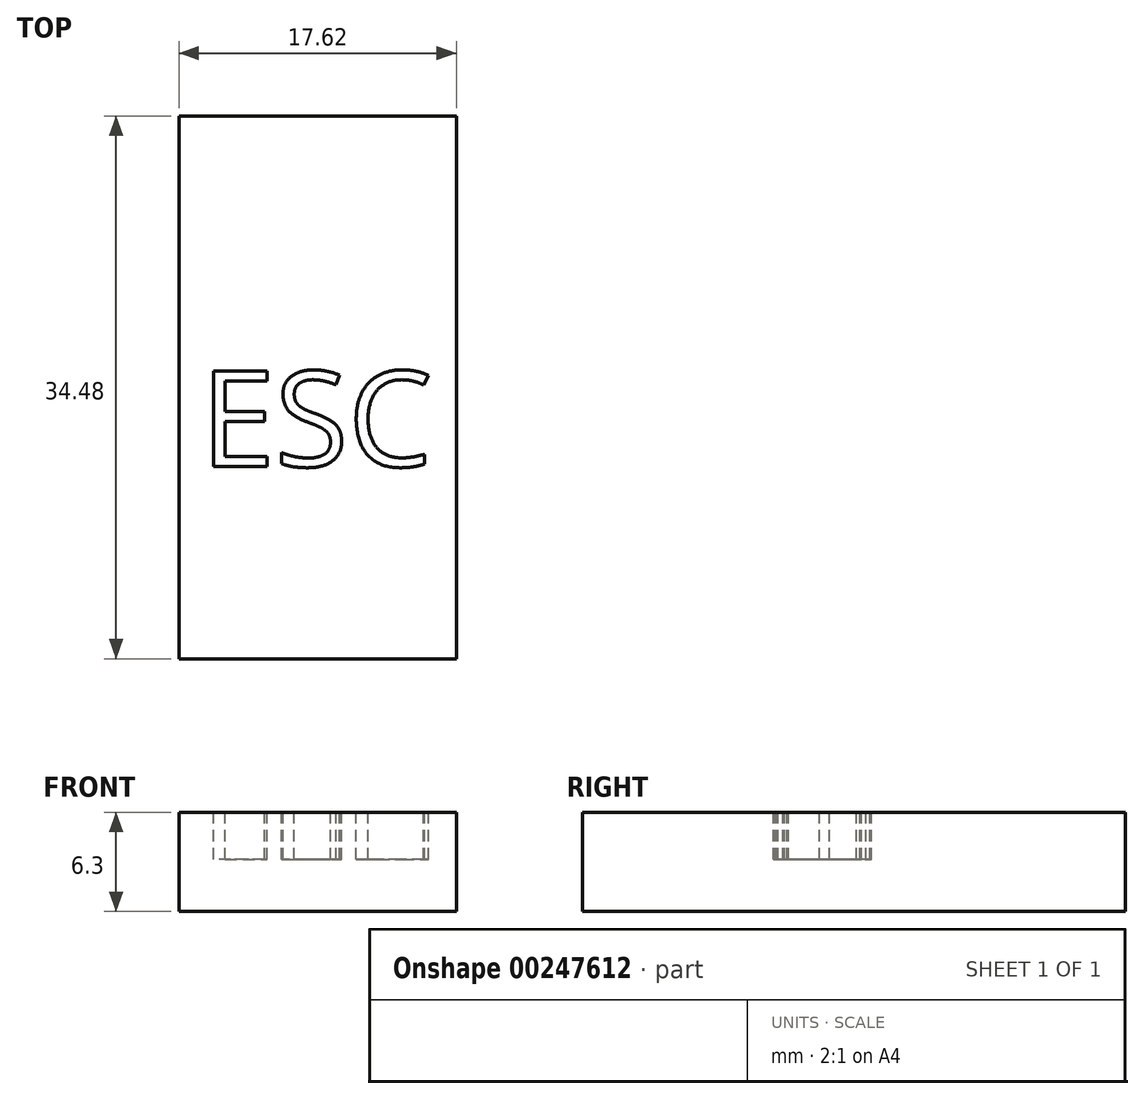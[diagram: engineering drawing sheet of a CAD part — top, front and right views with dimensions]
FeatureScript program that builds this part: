
annotation { "Feature Type Name" : "Feature", "Feature Type Description" : "" }
export const myFeature = defineFeature(function(context is Context, id is Id, definition is map)
    precondition{}
    {
        {
            var Q0;
            Q0=qCreatedBy(makeId("Top.planeOp"),FACE);
            var sketch = newSketch(context, id + "F0", { "sketchPlane" : qUnion([Q0])});
            skLineSegment(sketch, "E0.bottom", {"start": v(-8.8, 17.23) * mm, "end": v(8.81, 17.23) * mm});
            skLineSegment(sketch, "E0.top", {"start": v(-8.81, -17.23) * mm, "end": v(8.8, -17.23) * mm});
            skLineSegment(sketch, "E0.left", {"start": v(-8.8, 17.23) * mm, "end": v(-8.81, -17.23) * mm});
            skLineSegment(sketch, "E0.right", {"start": v(8.81, 17.23) * mm, "end": v(8.8, -17.23) * mm});
            skPoint(sketch, "E0.middle", {"position": v(0, 0) * mm});
            skSolve(sketch);
        }
        {
            var Q0;
            Q0 = qSketchRegion(id + "F0", true);
            extrude(context, id + "F1", {"entities" : qUnion([Q0]), "depth" : 6.3 * mm});
        }
        {
            var Q0;
            Q0=makeQuery(id+"F1.opExtrude","CAP_FACE",FACE,{"disambiguationData":[OSD([sQuery(id+"F0.wireOp",EDGE,"E0.bottom"),sQuery(id+"F0.wireOp",EDGE,"E0.top"),sQuery(id+"F0.wireOp",EDGE,"E0.left"),sQuery(id+"F0.wireOp",EDGE,"E0.right")])],"isStart":false});
            var sketch = newSketch(context, id + "F2", { "sketchPlane" : qUnion([Q0])});
            skText(sketch, "E1", { "text": "ESC", "fontName": "OpenSans-Regular.ttf"});
            const initialGuessF2  = {"E1": [-0.00743, -0.00502, 1, 0, 0.0061]};
            skSetInitialGuess(sketch, initialGuessF2);
            skSolve(sketch);
        }
        {
            var Q0;
            Q0 = qSketchRegion(id + "F2", true);
            extrude(context, id + "F3", {"entities" : qUnion([Q0]), "operationType" : NewBodyOperationType.REMOVE, "oppositeDirection" : true, "depth" : 3 * mm});
        }
    });
